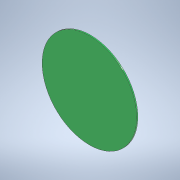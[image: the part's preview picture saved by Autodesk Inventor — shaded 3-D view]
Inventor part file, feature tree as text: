
AUTODESK INVENTOR PART (.ipt)
format: ipt  version: 2020.4 (Build 244396000, 396)  size: 95,744 bytes
history: native  units: mm
features: extrude x1, sketch x1
ambient origin geometry x8: Origin, YZ Plane, XZ Plane, XY Plane, X Axis, Y Axis, Z Axis, Center Point
bodies: Solid1 (feature_tree)
feature tree (2):
  extrude  "Extrusion1"  Depth=0.5mm TaperAngle=0.0deg
  sketch  "Sketch1"  dims[d0=42.0mm d1=0.5mm d2=0.0mm]
